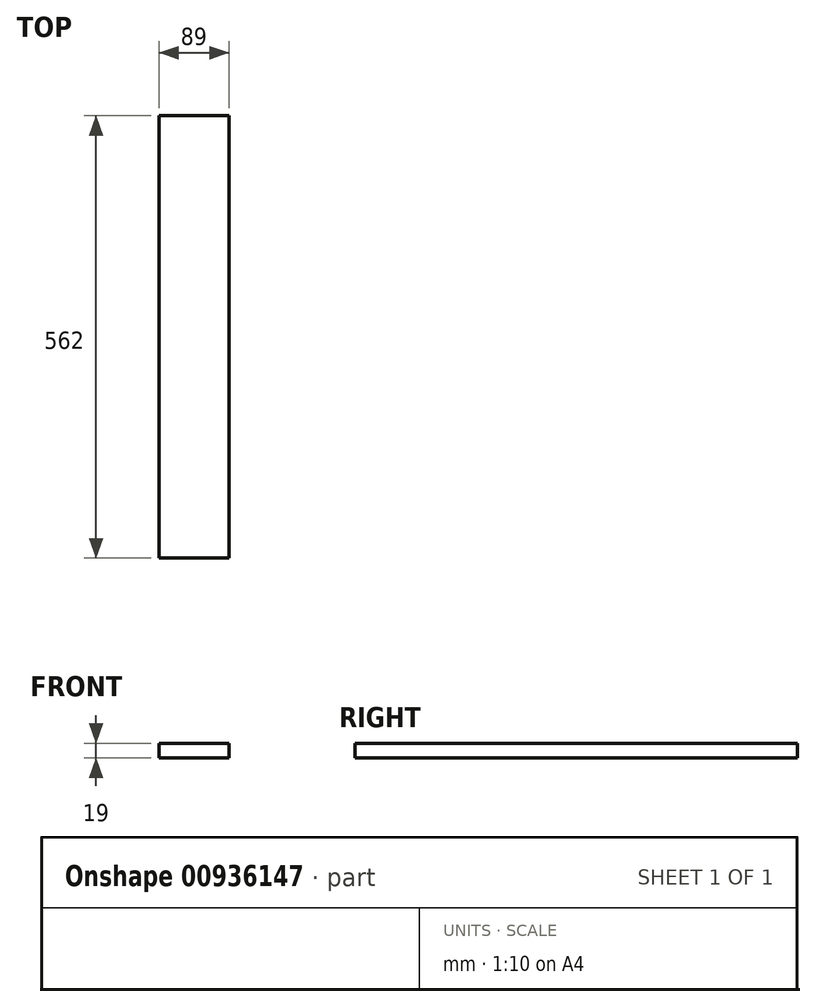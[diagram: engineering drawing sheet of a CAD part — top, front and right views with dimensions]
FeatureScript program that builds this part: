
annotation { "Feature Type Name" : "Feature", "Feature Type Description" : "" }
export const myFeature = defineFeature(function(context is Context, id is Id, definition is map)
    precondition{}
    {
        {
            var Q0;
            Q0=qCreatedBy(makeId("Front.planeOp"),FACE);
            var sketch = newSketch(context, id + "F0", { "sketchPlane" : qUnion([Q0])});
            skLineSegment(sketch, "E0.bottom", {"start": v(0, 0) * mm, "end": v(89, 0) * mm});
            skLineSegment(sketch, "E0.top", {"start": v(0, 19) * mm, "end": v(89, 19) * mm});
            skLineSegment(sketch, "E0.left", {"start": v(0, 0) * mm, "end": v(0, 19) * mm});
            skLineSegment(sketch, "E0.right", {"start": v(89, 0) * mm, "end": v(89, 19) * mm});
            skSolve(sketch);
        }
        {
            var Q0;
            Q0=makeQuery(id+"F0.imprint","IMPRINT",FACE,{"disambiguationData":[TD([[makeQuery(id+"F0.imprint","IMPRINT",EDGE,{"derivedFrom":sQuery(id+"F0.wireOp",EDGE,"E0.bottom")}),1.0]])]});
            extrude(context, id + "F1", {"entities" : qUnion([Q0]), "depth" : 562 * mm, "offsetDistance" : 25 * mm});
        }
    });
